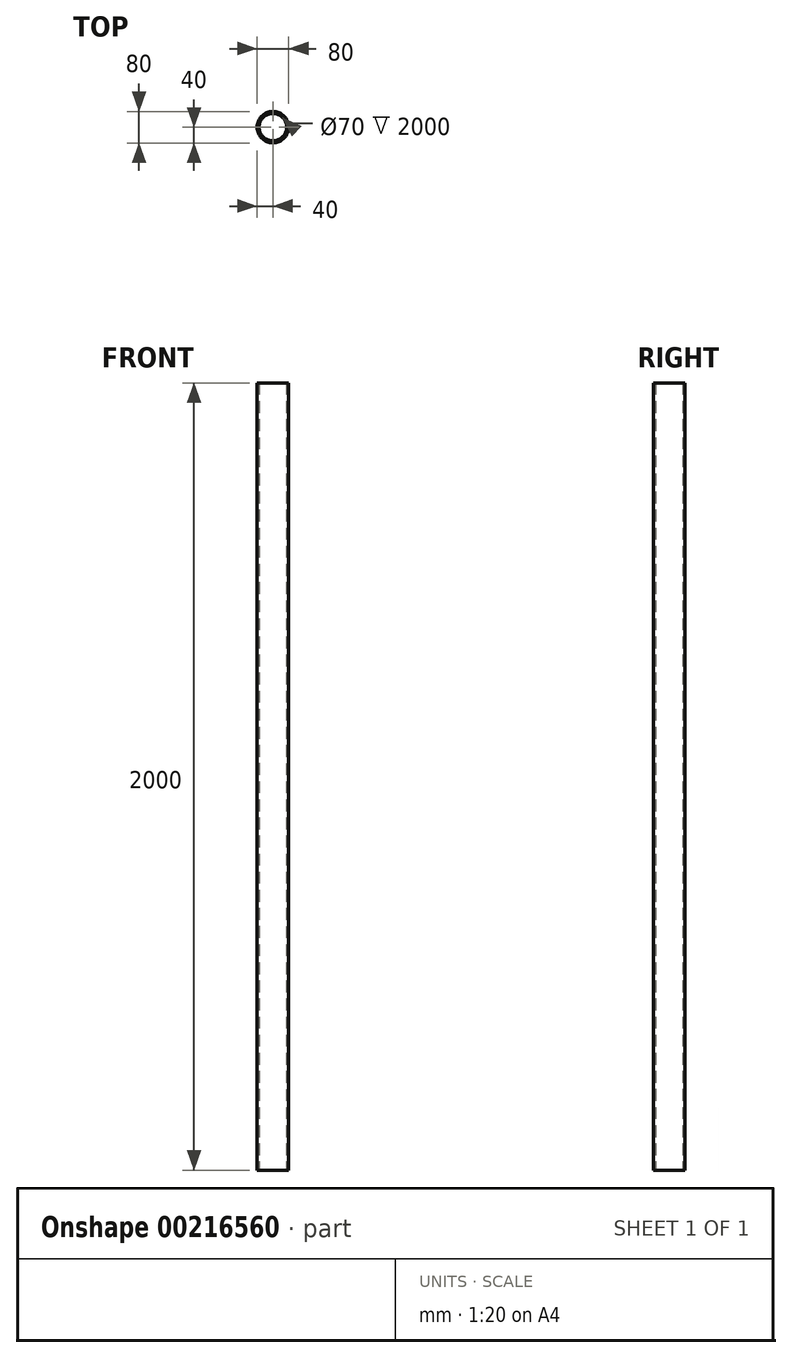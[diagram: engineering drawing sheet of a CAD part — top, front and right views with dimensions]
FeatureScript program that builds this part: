
annotation { "Feature Type Name" : "Feature", "Feature Type Description" : "" }
export const myFeature = defineFeature(function(context is Context, id is Id, definition is map)
    precondition{}
    {
        {
            var Q0;
            Q0=qCreatedBy(makeId("Top.planeOp"),FACE);
            var sketch = newSketch(context, id + "F0", { "sketchPlane" : qUnion([Q0])});
            skCircle(sketch, "E0", {"center": v(0, 0) * mm, "radius": 35 * mm});
            skCircle(sketch, "E1", {"center": v(0, 0) * mm, "radius": 40 * mm});
            skSolve(sketch);
        }
        {
            var Q0;
            Q0 = qSketchRegion(id + "F0", true);
            extrude(context, id + "F1", {"entities" : qUnion([Q0]), "depth" : 2000 * mm});
        }
    });
